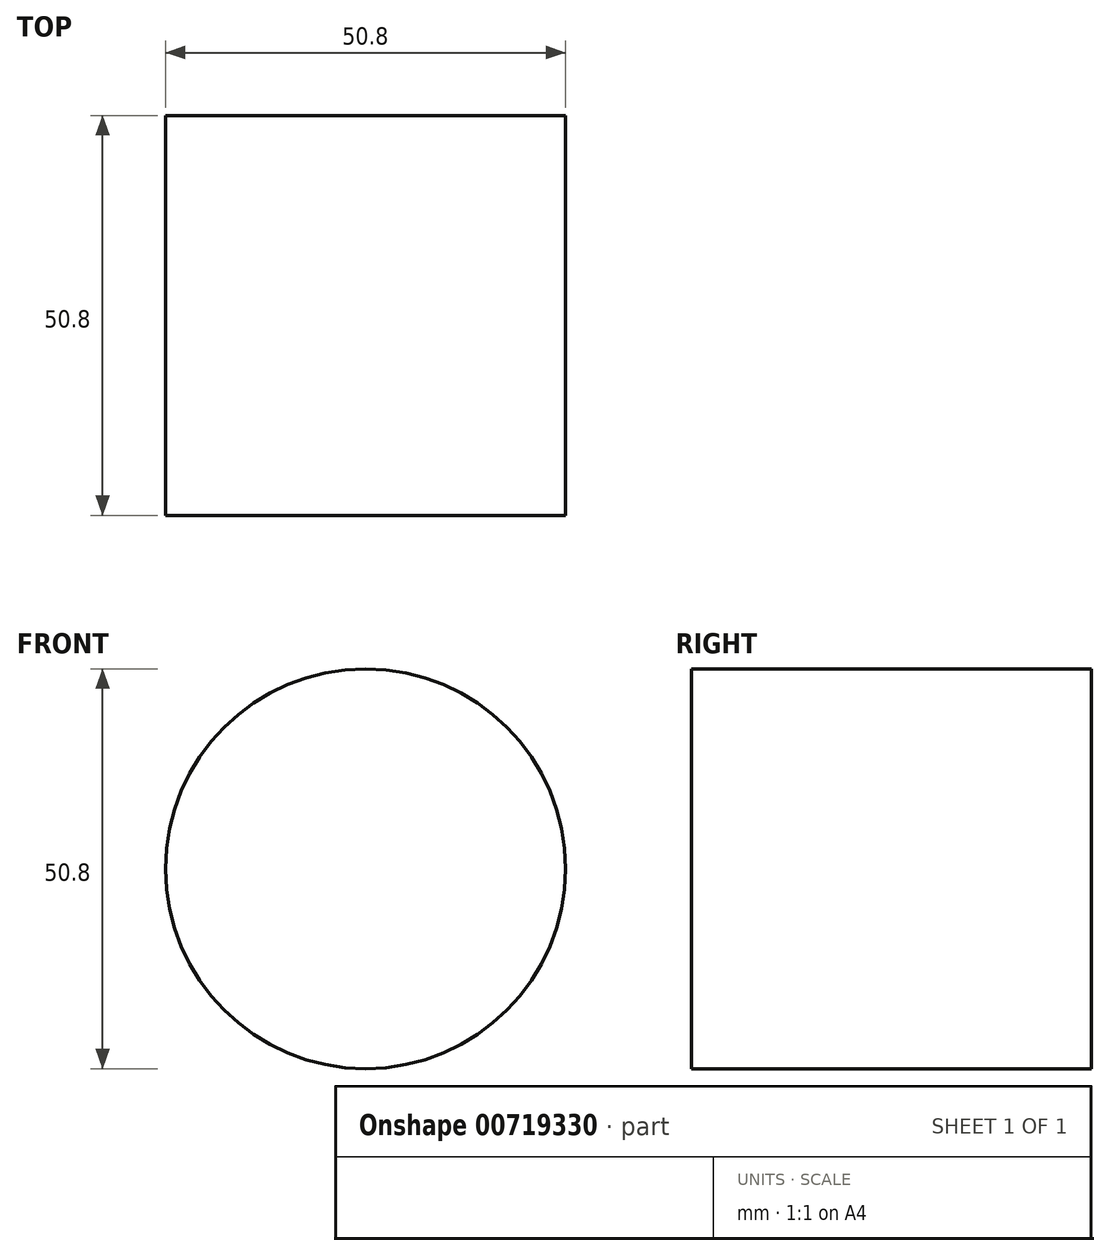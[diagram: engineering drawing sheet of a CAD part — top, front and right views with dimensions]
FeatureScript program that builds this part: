
annotation { "Feature Type Name" : "Feature", "Feature Type Description" : "" }
export const myFeature = defineFeature(function(context is Context, id is Id, definition is map)
    precondition{}
    {
        {
            var Q0;
            Q0=qCreatedBy(makeId("Front.planeOp"),FACE);
            var sketch = newSketch(context, id + "F0", { "sketchPlane" : qUnion([Q0])});
            skCircle(sketch, "E0", {"center": v(0, 0) * mm, "radius": 25.4 * mm});
            skSolve(sketch);
        }
        {
            var Q0;
            Q0 = qSketchRegion(id + "F0", true);
            extrude(context, id + "F1", {"entities" : qUnion([Q0]), "endBound" : BoundingType.SYMMETRIC, "depth" : 50.8 * mm, "offsetDistance" : 25.4 * mm});
        }
    });
